# Revit family: Digital_Media-Honeywell-Amplifier-580231(32)
name_source: partatom
category: Electrical Equipment
revit_build: Autodesk Revit 2017 (Build: 20160225_1515(x64)
units: mm (PartAtom-declared; Revit-internal decimal feet)

## family parameters
Cut with Voids When Loaded = No
Host = Face
OmniClass Number = 23.85.50.00
OmniClass Title = Communication Systems
Part Type = Other Panel
Room Calculation Point = No
Round Connector Dimension = Use Diameter
Shared = No

## types (2) — shared parameters
Ambient Temperature = -5 °C ... 55 °C
Apparent Load = 0 VA
Default Elevation = 1219 mm
Depth = 402 mm  [stored 1.3189 ft]
Finish = Metal - Honeywell - Stainless Steel - Black
Frequency = 50 Hz
Height = 89 mm  [stored 0.291995 ft]
Load Sub-Classification = No
Manufacturer = Honeywell International
Manufacturer Fax Number = 02131/40615-606
Number of Poles = 1
Power Factor = 1
Product Documentation Link = https://www.esser-systems.com
Product Name = Power amplifier
Product Page URL = https://www.esser-systems.com
Rated Frequency = 50 ... 60 Hz
Rated Voltage = 230 V AC
Storage Temperature = -10 °C ... 55 °C
URL = www.esser-systems.com
Utility = No
Version = 2017 - v1.0a
Voltage = 250
Width = 482 mm  [stored 1.58136 ft]

## per-type parameters (varying)
| type | Air Humidity | Constraints | Description | Model | Power Output | Rated Load Current | Rated current | Wattage | Watts | Weight |
| Power amplifier 2XD250 - 580231 | 0 ... 93 % | 1 | Power amplifier 2XD250 | 580231 | 2 x 250 W | 3 A | 2.8 A | 250 W | 250 W | 16.50 kgf |
| Power amplifier 2XD400 - 580232 | < 93 % | 2 | Power amplifier 2XD400 | 580232 | 2 x 400 W | 5 A | 4.5 A | 400 W | 400 W | 19.00 kgf |

note: [stored X ft] marks values corroborated as IEEE doubles in the binary element streams (Revit-internal decimal feet)

## geometry (parser evidence)
native form markers: Sweep x3
no freeform markers — native parametric forms only
